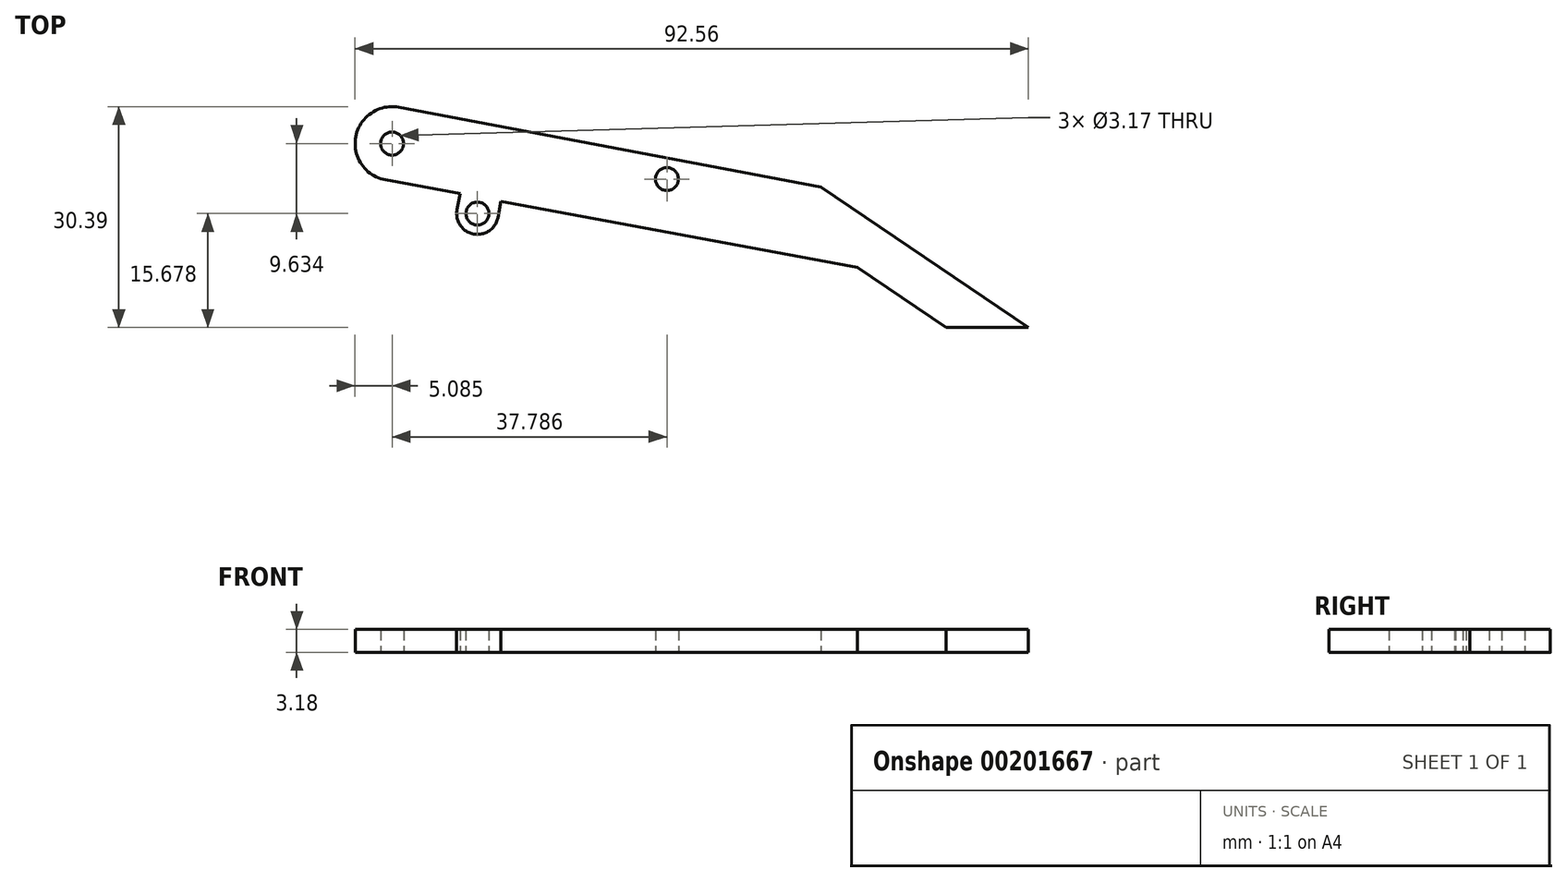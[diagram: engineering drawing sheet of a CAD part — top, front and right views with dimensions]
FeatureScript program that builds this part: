
annotation { "Feature Type Name" : "Feature", "Feature Type Description" : "" }
export const myFeature = defineFeature(function(context is Context, id is Id, definition is map)
    precondition{}
    {
        {
            var Q0;
            Q0=qCreatedBy(makeId("Top.planeOp"),FACE);
            var sketch = newSketch(context, id + "F0", { "sketchPlane" : qUnion([Q0])});
            skCircle(sketch, "E0", {"center": v(-34.24, 23.04) * mm, "radius": 5.08 * mm});
            skLineSegment(sketch, "E1", {"start": v(-33.3, 28.03) * mm, "end": v(24.72, 17.07) * mm});
            skLineSegment(sketch, "E2", {"start": v(24.72, 17.07) * mm, "end": v(53.24, -2.27) * mm});
            skLineSegment(sketch, "E3", {"start": v(-35.16, 18.05) * mm, "end": v(29.76, 5.98) * mm});
            skLineSegment(sketch, "E4", {"start": v(29.76, 5.98) * mm, "end": v(41.93, -2.27) * mm});
            skLineSegment(sketch, "E5", {"start": v(41.93, -2.27) * mm, "end": v(53.24, -2.27) * mm});
            skCircle(sketch, "E6", {"center": v(-34.24, 23.04) * mm, "radius": 1.59 * mm});
            skCircle(sketch, "E7", {"center": v(-22.5, 13.4) * mm, "radius": 1.59 * mm});
            skLineSegment(sketch, "E8", {"start": v(-24.9, 16.14) * mm, "end": v(-25.3, 13.93) * mm});
            skLineSegment(sketch, "E9", {"start": v(-25.3, 13.93) * mm, "end": v(-19.69, 12.89) * mm, "construction": true});
            skLineSegment(sketch, "E10", {"start": v(-19.69, 12.89) * mm, "end": v(-19.28, 15.1) * mm});
            skArc(sketch, "E11", {"start": v(-25.3, 13.93) * mm, "mid": v(-23.02, 10.6) * mm, "end": v(-19.69, 12.89) * mm});
            skCircle(sketch, "E12", {"center": v(3.55, 18.16) * mm, "radius": 1.59 * mm});
            skSolve(sketch);
        }
        {
            var Q0;
            Q0 = qSketchRegion(id + "F0", true);
            extrude(context, id + "F1", {"entities" : qUnion([Q0]), "depth" : 3.17 * mm});
        }
    });
